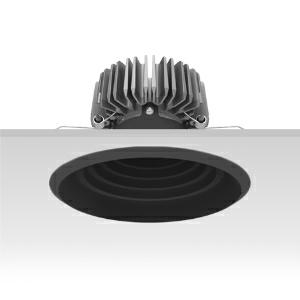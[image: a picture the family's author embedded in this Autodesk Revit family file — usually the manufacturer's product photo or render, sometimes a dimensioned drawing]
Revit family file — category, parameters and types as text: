
# Revit family: 3f_filippi_-_3f_reno_nero_spot_3f_filippi_-_31471_-_3f_reno_200_bk_4000-840_dali_spot
name_source: partatom
category: Lighting Fixtures
units: mm (PartAtom-declared; Revit-internal decimal feet)

## family parameters
Cut with Voids When Loaded = No
Host = Face
Light Source = No
Part Type = Normal
Room Calculation Point = No
Round Connector Dimension = Use Diameter
Shared = No

## types (1)
- 3F Filippi - 3F Reno Nero Spot (1 x LED, 4287 lm, 36 W, 4000 K)
    Apparent Load = 36 VA
    Approval mark = CE
    CIE Flux Codes = 93 100 100 100 100
    Color Rendering = 80
    Color Temperature = 4000 K
    Control Gear = Electronic transformer
    Default Elevation = 1800 mm
    Description = ILLUMINOTECHNICAL
Luminous efficiency 100% (DLOR 100%, ULOR 0%).
Initial luminous flux of the luminaire 4287 lm.
Symmetrical spot distribution.
Installation Interdistance Transv.D = 0.60 x hu - Long.D = 0.60 x hu.
Tabular UGR (CIE 117 - 4H-8H; S=0.25H; 70/50/20): RUG 17.8 - 17.7.
Beam angle: 37° - 37°.
Luminous efficacy 119 lm/W.
Lifetime (L90/B10): 30000 h. (tq+25°C)
Lifetime (L85/B10): 50000 h. (tq+25°C)
Lifetime (L70/B10): 80000 h. (tq+25°C)
Sudden decreased luminous flux after 50000 hours: 0% (C0).
Photobiological safety in compliance with IEC/TR 62778: RG1 low risk, (IEC 62471).
In compliance with IEC/EN 62722-2-1 - IEC/EN 62717 standards.

SOURCE
Compact LED module 4000/840.
Energy efficiency class (UE 2019/2020 - UE 2019/2015): D.
CIE 13.3 Colour rendering index: CRI >80 (R9 <50%).
IES TM-30 Fidelity Index: Rf = 84 Rg = 95.
CCT nominal colour temperature 4000 K.
Colour initial tolerance (MacAdam): SDCM 3.
Zhaga Book 3 compliant.

MECHANICAL
Passive heat dissipator in die-casting aluminium, oversized, for optimum thermal management of the LED module.
Parabolic element with graduated/concentric rings in black polycarbonate.
Internal specular metallic louvre to optimise control of the luminous flux in polycarbonate.
Transparent external lens with glossy and satin differentiated surfaces, with a cooling and anti-insect system in methacrylate (PMMA).
Fastening spring clips in stainless steel.
Dimensions: diameter 216 mm, height 142 mm. Weight 1.515 kg.
IP44 protection degree for exposed part, IP20 for recessed part.
Mechanical strength to impacts IK04 (0.5 joule).
Glow-wire test resistance 650°C.

ELECTRICAL
Wiring on a separate unit.
Halogen Free DALI-2 DATI (Parts 251, 252, 253), PUSH-DIM, electronic wiring 230V-50/60Hz, power factor 0.97 at full load, THD <25%, constant output current, SELV, class II, 1 driver, 1 DALI addresse.
Power of the luminaire 36 W.
ENEC - CE.
SAFE FLICKER: PstLM=<1 and SVM=<0.4 (IEC TR 61547-1 and IEC TR 63158), to ensure a more comfortable and safe light.
Luminaire compliant with EN 60598-2-22 for power supply from a centralised emergency system CPSS (Central Power Supply System), not incorporated in the luminaire - high risk areas excluded. The default power and flux are 100% in AC and 100% in DC.
Ambient temperature from 0°C to +25°C.
Temperature class T6 max 85°C.
Relative humidity UR: <85%.

INSTALLATION
Pull-up recessed fitting.
False ceiling carving: 200 mm.
All accessories dedicated to this product are available on the Catalog and on our website www.3F-Filippi.com.

APPLICATIONS
Environments: architectural, commercial, exhibition areas, transit areas, corridors, shops, display windows, service areas.
In false ceilings with narrow voids.

LIGHT MANAGEMENT
Recommended minimum setting: 10%.
The luminaire, equipped with (DALI-2 DATI) driver, can be controlled manually with 3F Easy Dim technology or automatically/manually with wired or wireless DALI/D2D control systems.
The D2D driver guarantees interoperability with other devices with the same certification by making the following information available:
Device Data (Part 251), Energy Report (Part 252), Diagnosis & Maintenance (Part 253).
In electrical systems without a regulation system (manual or automatic) and DALI bus, a suitable jumper must be made on the DA-DA terminals of the appliance.

WARNING
Luminaire designed for disposal/recycling at end-of-life.
Replaceable (LED only) light source by a professional. Replaceable control gear by a professional.
    Height = 0 mm  [stored 0 ft]
    Lamp = 1 x LED
    Lamp Light Flux = 4287 lm
    Lamp Power = 36 W
    Lamp count = 1
    Length = 216 mm
    Lifetime = 50000 h
    Luminous efficacy = 119 lm/W
    Manufacturer = 3F Filippi
    ModVariant = No
    Model = 3F Filippi - 31471 - 3F Reno 200 BK 4000-840 DALI SPOT
    Mounting Place = Ceiling
    Mounting Type = Recessed
    Number of Poles = 1
    OnlyDefault = Yes
    Power Factor = 1
    Product Name = 3F Filippi - 3F Reno Nero Spot
    Product group = recessed luminaire
    ProductGroupID = 4
    Protection Class = Protection class II
    Protection Degree = IP 20
    RLX_Detail_Level = 1
    RLX_Emergency_Light_Flux = 0 lm
    RLX_Emergency_Type = 0
    RLX_Emergency_Type_DB = No
    RlxData = <blob elided: 95933 chars, md5=f2a0089c>
    Socket = socket
    Standby Power = 0 W
    System Light Flux = 4287 lm
    System Power = 36 W
    Type Comments = Product without accessories
    Type Image = 3ffilippi_3f_reno_200_bk_2500_3000_4000.jpg
    URL = http://relux.com
    VarID = ---
    Voltage = 0 V
    Weight = 0.00 kg
    Width = 0 mm  [stored 0 ft]

note: [stored X ft] marks values corroborated as IEEE doubles in the binary element streams (Revit-internal decimal feet)

## geometry (parser evidence)
native form markers: Blend x4, Sweep x8
no freeform markers — native parametric forms only
